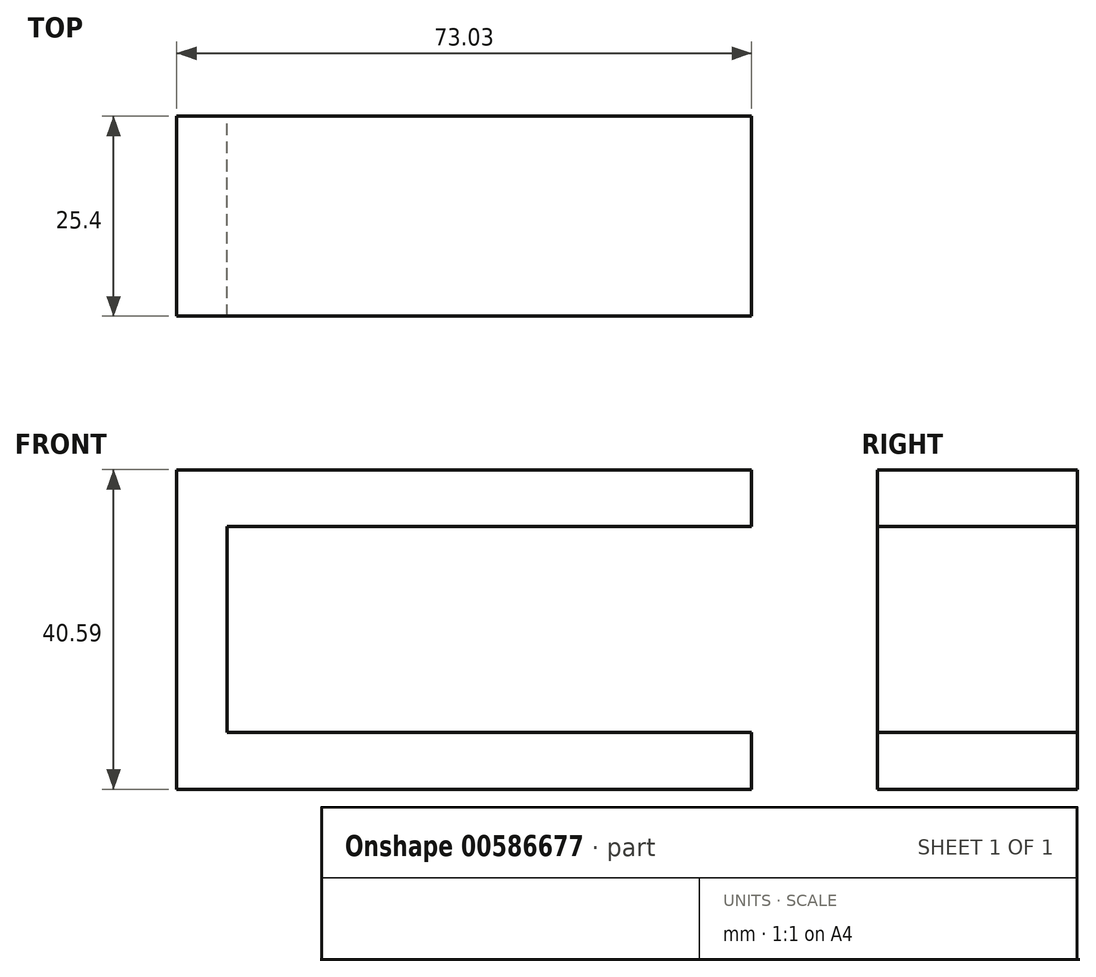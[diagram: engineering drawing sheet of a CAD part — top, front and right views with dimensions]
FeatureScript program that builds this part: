
annotation { "Feature Type Name" : "Feature", "Feature Type Description" : "" }
export const myFeature = defineFeature(function(context is Context, id is Id, definition is map)
    precondition{}
    {
        {
            var Q0;
            Q0=qCreatedBy(makeId("Front.planeOp"),FACE);
            var sketch = newSketch(context, id + "F0", { "sketchPlane" : qUnion([Q0])});
            skLineSegment(sketch, "E0.bottom", {"start": v(0, 0) * mm, "end": v(73.03, 0) * mm});
            skLineSegment(sketch, "E0.top", {"start": v(0, -7.22) * mm, "end": v(73.03, -7.22) * mm});
            skLineSegment(sketch, "E0.left", {"start": v(0, 0) * mm, "end": v(0, -7.22) * mm});
            skLineSegment(sketch, "E0.right", {"start": v(73.03, 0) * mm, "end": v(73.03, -7.22) * mm});
            skLineSegment(sketch, "E1.bottom", {"start": v(0, 33.37) * mm, "end": v(73.03, 33.37) * mm});
            skLineSegment(sketch, "E1.top", {"start": v(0, 26.15) * mm, "end": v(73.03, 26.15) * mm});
            skLineSegment(sketch, "E1.left", {"start": v(0, 33.37) * mm, "end": v(0, 26.15) * mm});
            skLineSegment(sketch, "E1.right", {"start": v(73.03, 33.37) * mm, "end": v(73.03, 26.15) * mm});
            skLineSegment(sketch, "E2.bottom", {"start": v(0, 33.37) * mm, "end": v(6.38, 33.37) * mm});
            skLineSegment(sketch, "E2.top", {"start": v(0, -7.22) * mm, "end": v(6.38, -7.22) * mm});
            skLineSegment(sketch, "E2.left", {"start": v(0, 33.37) * mm, "end": v(0, -7.22) * mm});
            skLineSegment(sketch, "E2.right", {"start": v(6.38, 33.37) * mm, "end": v(6.38, -7.22) * mm});
            skSolve(sketch);
        }
        {
            var Q0;
            Q0 = qSketchRegion(id + "F0", true);
            extrude(context, id + "F1", {"entities" : qUnion([Q0]), "depth" : 25.4 * mm, "offsetDistance" : 25.4 * mm});
        }
    });
